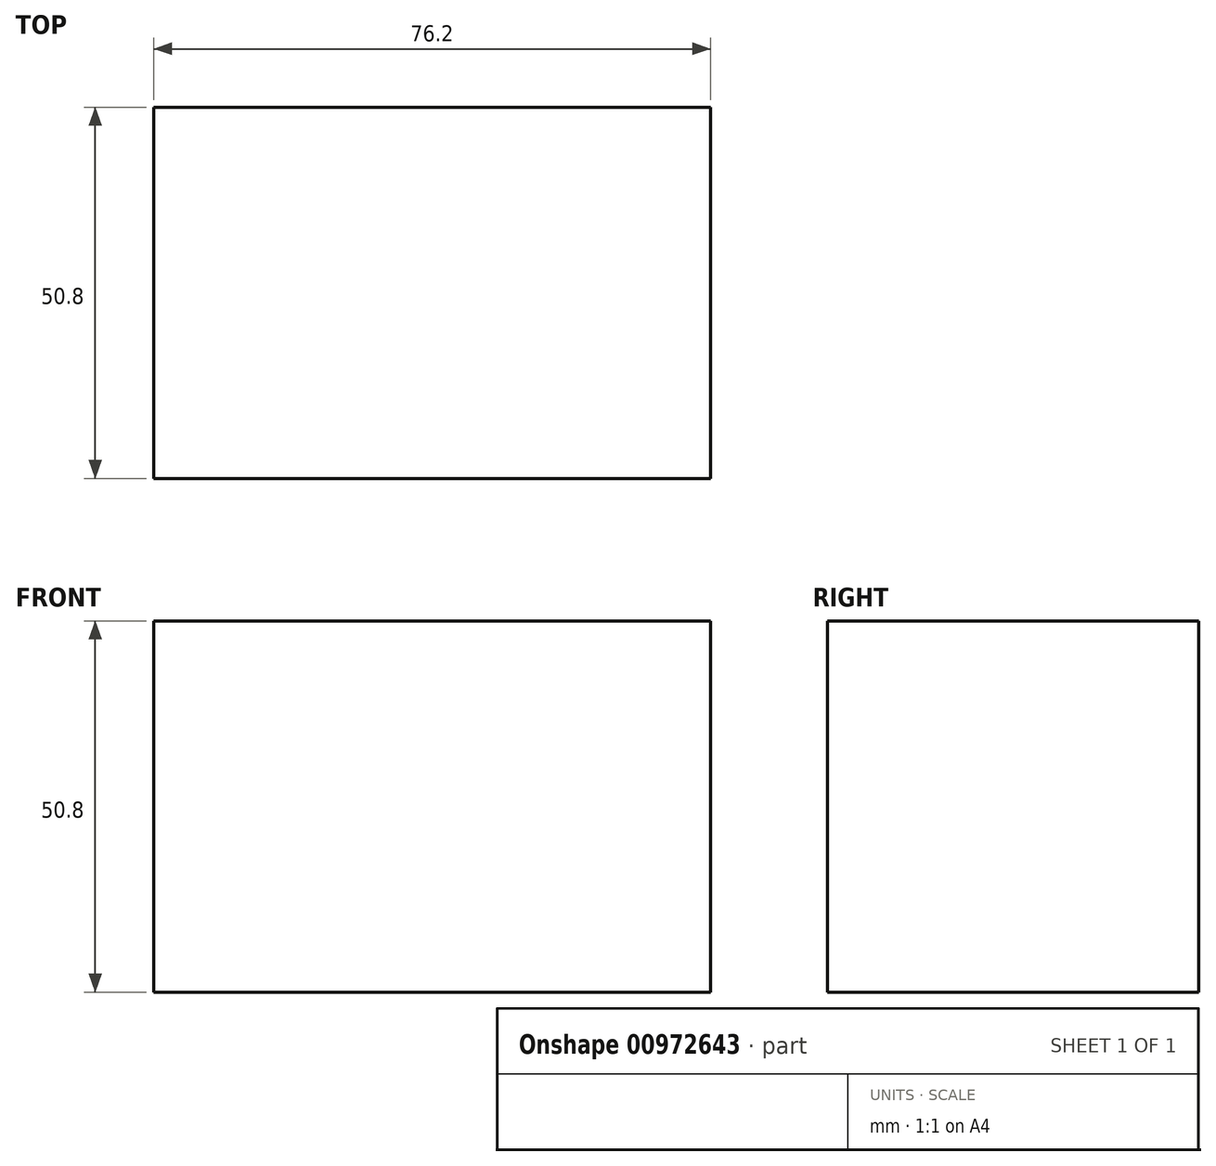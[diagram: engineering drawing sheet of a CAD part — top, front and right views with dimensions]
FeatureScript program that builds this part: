
annotation { "Feature Type Name" : "Feature", "Feature Type Description" : "" }
export const myFeature = defineFeature(function(context is Context, id is Id, definition is map)
    precondition{}
    {
        {
            var Q0;
            Q0=qCreatedBy(makeId("Top.planeOp"),FACE);
            var sketch = newSketch(context, id + "F0", { "sketchPlane" : qUnion([Q0])});
            skLineSegment(sketch, "E0.bottom", {"start": v(-38.1, 25.4) * mm, "end": v(38.1, 25.4) * mm});
            skLineSegment(sketch, "E0.top", {"start": v(-38.1, -25.4) * mm, "end": v(38.1, -25.4) * mm});
            skLineSegment(sketch, "E0.left", {"start": v(-38.1, 25.4) * mm, "end": v(-38.1, -25.4) * mm});
            skLineSegment(sketch, "E0.right", {"start": v(38.1, 25.4) * mm, "end": v(38.1, -25.4) * mm});
            skPoint(sketch, "E0.middle", {"position": v(0, 0) * mm});
            skSolve(sketch);
        }
        {
            var Q0;
            Q0=makeQuery(id+"F0.imprint","IMPRINT",FACE,{"disambiguationData":[TD([[makeQuery(id+"F0.imprint","IMPRINT",EDGE,{"derivedFrom":sQuery(id+"F0.wireOp",EDGE,"E0.bottom")}),-1.0]])]});
            var sketch = newSketch(context, id + "F1", { "sketchPlane" : qUnion([Q0])});
            skCircle(sketch, "E1", {"center": v(0, 0) * mm, "radius": 9.53 * mm});
            skSolve(sketch);
        }
        {
            var Q0;
            Q0=makeQuery(id+"F0.imprint","IMPRINT",FACE,{"disambiguationData":[TD([[makeQuery(id+"F0.imprint","IMPRINT",EDGE,{"derivedFrom":sQuery(id+"F0.wireOp",EDGE,"E0.bottom")}),-1.0]])]});
            extrude(context, id + "F2", {"entities" : qUnion([Q0]), "depth" : 25.4 * mm, "offsetDistance" : 25.4 * mm});
        }
        {
            var Q0;
            Q0=makeQuery(id+"F2.opExtrude","CAP_FACE",FACE,{"disambiguationData":[OSD([sQuery(id+"F0.wireOp",EDGE,"E0.bottom"),sQuery(id+"F0.wireOp",EDGE,"E0.top"),sQuery(id+"F0.wireOp",EDGE,"E0.left"),sQuery(id+"F0.wireOp",EDGE,"E0.right")])],"isStart":false});
            var Q1;
            Q1=sQuery(id+"F1.wireOp",EDGE,"E1");
            extrude(context, id + "F3", {"entities" : qUnion([Q0]), "operationType" : NewBodyOperationType.ADD, "surfaceEntities" : qUnion([Q1]), "depth" : 25.4 * mm, "offsetDistance" : 25.4 * mm});
        }
    });
